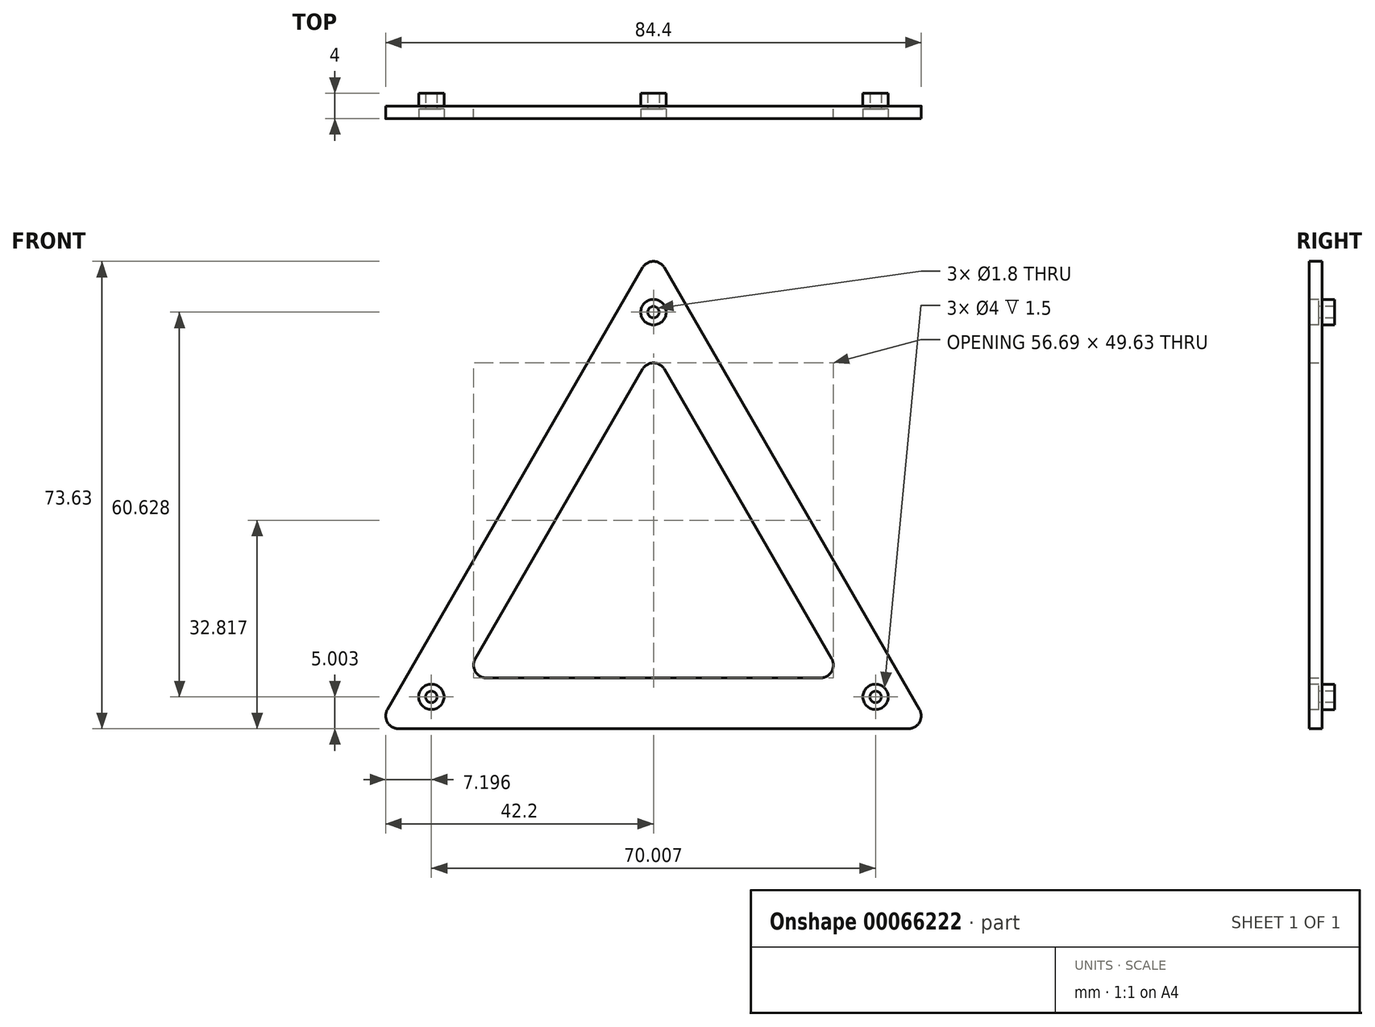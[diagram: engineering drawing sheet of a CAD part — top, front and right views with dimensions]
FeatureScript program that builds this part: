
annotation { "Feature Type Name" : "Feature", "Feature Type Description" : "" }
export const myFeature = defineFeature(function(context is Context, id is Id, definition is map)
    precondition{}
    {
        {
            var Q0;
            Q0=qCreatedBy(makeId("Front.planeOp"),FACE);
            var sketch = newSketch(context, id + "F0", { "sketchPlane" : qUnion([Q0])});
            skLineSegment(sketch, "E0.2", {"start": v(1.73, 31.51) * mm, "end": v(28.08, -14.12) * mm});
            skLineSegment(sketch, "E0.1", {"start": v(-1.73, 31.51) * mm, "end": v(-28.08, -14.12) * mm});
            skArc(sketch, "E1.0", {"start": v(-1.73, 47.51) * mm, "mid": v(0, 48.51) * mm, "end": v(1.73, 47.51) * mm});
            skArc(sketch, "E0.0", {"start": v(-1.73, 31.51) * mm, "mid": v(0, 32.51) * mm, "end": v(1.73, 31.51) * mm});
            skArc(sketch, "E0.5", {"start": v(-26.34, -17.12) * mm, "mid": v(-28.08, -16.12) * mm, "end": v(-28.08, -14.12) * mm});
            skArc(sketch, "E0.3", {"start": v(28.08, -14.12) * mm, "mid": v(28.08, -16.12) * mm, "end": v(26.34, -17.12) * mm});
            skLineSegment(sketch, "E0.4", {"start": v(26.34, -17.12) * mm, "end": v(-26.34, -17.12) * mm});
            skArc(sketch, "E1.2", {"start": v(41.93, -22.12) * mm, "mid": v(41.93, -24.12) * mm, "end": v(40.2, -25.12) * mm});
            skArc(sketch, "E1.1", {"start": v(-40.2, -25.12) * mm, "mid": v(-41.93, -24.12) * mm, "end": v(-41.93, -22.12) * mm});
            skLineSegment(sketch, "E2", {"start": v(41.93, -22.12) * mm, "end": v(1.73, 47.51) * mm});
            skLineSegment(sketch, "E3", {"start": v(-1.73, 47.51) * mm, "end": v(-41.93, -22.12) * mm});
            skLineSegment(sketch, "E4", {"start": v(-40.2, -25.12) * mm, "end": v(40.2, -25.12) * mm});
            skSolve(sketch);
        }
        {
            var Q0;
            Q0=qSketchRegion(id+"F0",true);
            extrude(context, id + "F1", {"entities" : qUnion([Q0]), "depth" : 2 * mm});
        }
        {
            var Q0;
            Q0=makeQuery(id+"F1.opExtrude","CAP_FACE",FACE,{"disambiguationData":[OSD([sQuery(id+"F0.wireOp",EDGE,"E0.2"),sQuery(id+"F0.wireOp",EDGE,"E0.1"),sQuery(id+"F0.wireOp",EDGE,"E1.0"),sQuery(id+"F0.wireOp",EDGE,"E0.0"),sQuery(id+"F0.wireOp",EDGE,"E0.5"),sQuery(id+"F0.wireOp",EDGE,"E0.3"),sQuery(id+"F0.wireOp",EDGE,"E0.4"),sQuery(id+"F0.wireOp",EDGE,"E1.2"),sQuery(id+"F0.wireOp",EDGE,"E1.1"),sQuery(id+"F0.wireOp",EDGE,"E2"),sQuery(id+"F0.wireOp",EDGE,"E3"),sQuery(id+"F0.wireOp",EDGE,"E4")])],"isStart":true});
            var sketch = newSketch(context, id + "F2", { "sketchPlane" : qUnion([Q0])});
            skCircle(sketch, "E5", {"center": v(0, 40.51) * mm, "radius": 0.9 * mm});
            skCircle(sketch, "E6", {"center": v(0, 40.51) * mm, "radius": 2 * mm});
            skCircle(sketch, "E7", {"center": v(-35, -20.12) * mm, "radius": 2 * mm});
            skCircle(sketch, "E8", {"center": v(-35, -20.12) * mm, "radius": 0.9 * mm});
            skCircle(sketch, "E9", {"center": v(35, -20.12) * mm, "radius": 2 * mm});
            skCircle(sketch, "E10", {"center": v(35, -20.12) * mm, "radius": 0.9 * mm});
            skLineSegment(sketch, "E11", {"start": v(-41.93, -24.12) * mm, "end": v(-28.08, -16.12) * mm, "construction": true});
            skLineSegment(sketch, "E12", {"start": v(-28.08, -16.12) * mm, "end": v(-35, -20.12) * mm, "construction": true});
            skLineSegment(sketch, "E13", {"start": v(28.08, -16.12) * mm, "end": v(41.93, -24.12) * mm, "construction": true});
            skLineSegment(sketch, "E14", {"start": v(41.93, -24.12) * mm, "end": v(35, -20.12) * mm, "construction": true});
            skLineSegment(sketch, "E15", {"start": v(0, 48.51) * mm, "end": v(0, 32.51) * mm, "construction": true});
            skLineSegment(sketch, "E16", {"start": v(0, 32.51) * mm, "end": v(0, 40.51) * mm, "construction": true});
            skSolve(sketch);
        }
        {
            var Q0;
            Q0=qSketchRegion(id+"F2",true);
            extrude(context, id + "F3", {"entities" : qUnion([Q0]), "operationType" : NewBodyOperationType.ADD, "depth" : 2 * mm});
        }
        {
            var Q0;
            Q0=makeQuery(id+"F1.opExtrude","CAP_FACE",FACE,{"disambiguationData":[OSD([sQuery(id+"F0.wireOp",EDGE,"E0.2"),sQuery(id+"F0.wireOp",EDGE,"E0.1"),sQuery(id+"F0.wireOp",EDGE,"E1.0"),sQuery(id+"F0.wireOp",EDGE,"E0.0"),sQuery(id+"F0.wireOp",EDGE,"E0.5"),sQuery(id+"F0.wireOp",EDGE,"E0.3"),sQuery(id+"F0.wireOp",EDGE,"E0.4"),sQuery(id+"F0.wireOp",EDGE,"E1.2"),sQuery(id+"F0.wireOp",EDGE,"E1.1"),sQuery(id+"F0.wireOp",EDGE,"E2"),sQuery(id+"F0.wireOp",EDGE,"E3"),sQuery(id+"F0.wireOp",EDGE,"E4")])],"isStart":false});
            var sketch = newSketch(context, id + "F4", { "sketchPlane" : qUnion([Q0])});
            skCircle(sketch, "E17.0", {"center": v(35, -20.12) * mm, "radius": 0.9 * mm, "construction": true});
            skCircle(sketch, "E17.1", {"center": v(-35, -20.12) * mm, "radius": 0.9 * mm, "construction": true});
            skCircle(sketch, "E17.2", {"center": v(0, 40.51) * mm, "radius": 0.9 * mm, "construction": true});
            skSolve(sketch);
        }
        {
            var Q0;
            Q0=sQuery(id+"F4.wireOp",VERTEX,"E17.2.center");
            var Q1;
            Q1=sQuery(id+"F4.wireOp",VERTEX,"E17.1.center");
            var Q2;
            Q2=sQuery(id+"F4.wireOp",VERTEX,"E17.0.center");
            var Q3;
            Q3=makeQuery(id+"F1.opExtrude","SWEPT_BODY",BODY,{"disambiguationData":[OSD([sQuery(id+"F0.wireOp",EDGE,"E0.2"),sQuery(id+"F0.wireOp",EDGE,"E0.1"),sQuery(id+"F0.wireOp",EDGE,"E1.0"),sQuery(id+"F0.wireOp",EDGE,"E0.0"),sQuery(id+"F0.wireOp",EDGE,"E0.5"),sQuery(id+"F0.wireOp",EDGE,"E0.3"),sQuery(id+"F0.wireOp",EDGE,"E0.4"),sQuery(id+"F0.wireOp",EDGE,"E1.2"),sQuery(id+"F0.wireOp",EDGE,"E1.1"),sQuery(id+"F0.wireOp",EDGE,"E2"),sQuery(id+"F0.wireOp",EDGE,"E3"),sQuery(id+"F0.wireOp",EDGE,"E4")])]});
            hole(context, id + "F5", {"style" : HoleStyle.C_BORE, "holeDiameter" : 1.8 * mm, "cBoreDiameter" : 4 * mm, "cBoreDepth" : 1.5 * mm, "endStyle" : HoleEndStyle.THROUGH, "locations" : qUnion([Q0, Q1, Q2]), "scope" : qUnion([Q3])});
        }
    });
